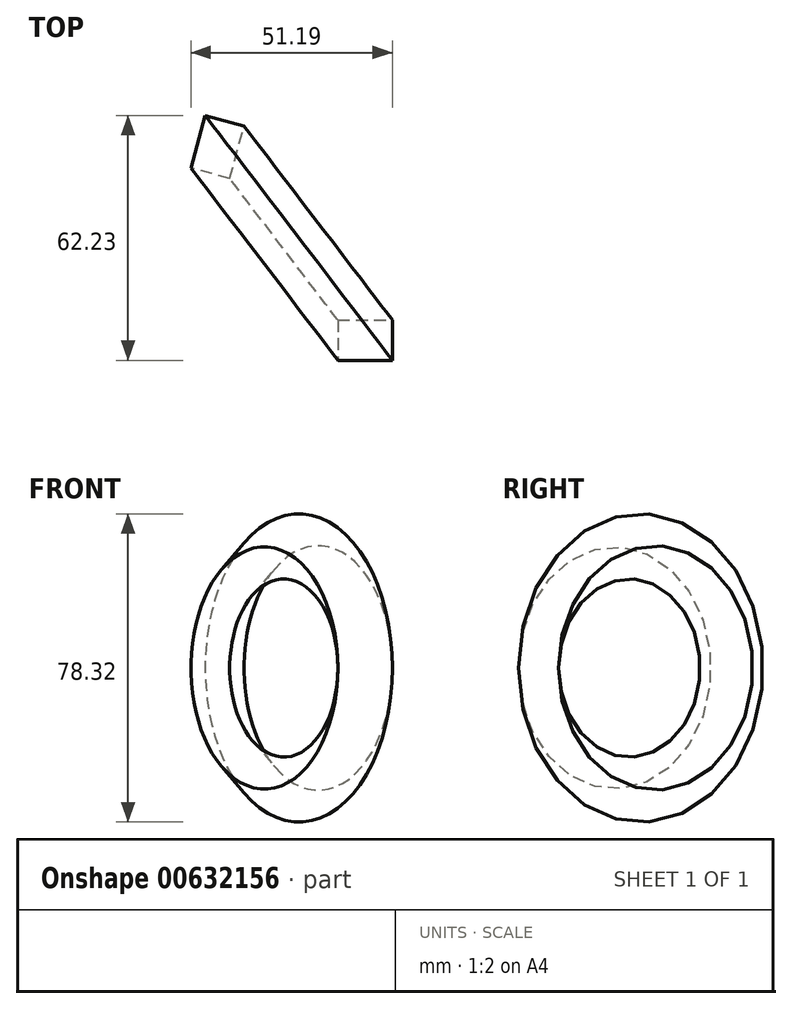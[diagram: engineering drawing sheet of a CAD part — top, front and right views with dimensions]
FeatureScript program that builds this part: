
annotation { "Feature Type Name" : "Feature", "Feature Type Description" : "" }
export const myFeature = defineFeature(function(context is Context, id is Id, definition is map)
    precondition{}
    {
        {
            var Q0;
            Q0=qCreatedBy(makeId("Top.planeOp"),FACE);
            var sketch = newSketch(context, id + "F0", { "sketchPlane" : qUnion([Q0])});
            skLineSegment(sketch, "E0.bottom", {"start": v(27.23, -28.42) * mm, "end": v(13.39, -28.42) * mm});
            skLineSegment(sketch, "E0.top", {"start": v(27.23, -18.2) * mm, "end": v(13.39, -18.2) * mm});
            skLineSegment(sketch, "E0.left", {"start": v(27.23, -28.42) * mm, "end": v(27.23, -18.2) * mm});
            skLineSegment(sketch, "E0.right", {"start": v(13.39, -28.42) * mm, "end": v(13.39, -18.2) * mm});
            skPoint(sketch, "E0.middle", {"position": v(20.3, -23.31) * mm});
            skLineSegment(sketch, "E1", {"start": v(-22.7, -17.3) * mm, "end": v(35.94, 27.52) * mm});
            skSolve(sketch);
        }
        {
            var Q0;
            Q0=makeQuery(id+"F0.imprint","IMPRINT",FACE,{"disambiguationData":[TD([[makeQuery(id+"F0.imprint","IMPRINT",EDGE,{"derivedFrom":sQuery(id+"F0.wireOp",EDGE,"E0.bottom")}),-1.0]])]});
            var Q1;
            Q1=sQuery(id+"F0.wireOp",EDGE,"E1");
            revolve(context, id + "F1", {"entities" : qUnion([Q0]), "axis" : qUnion([Q1]), "revolveType" : RevolveType.FULL});
        }
    });
